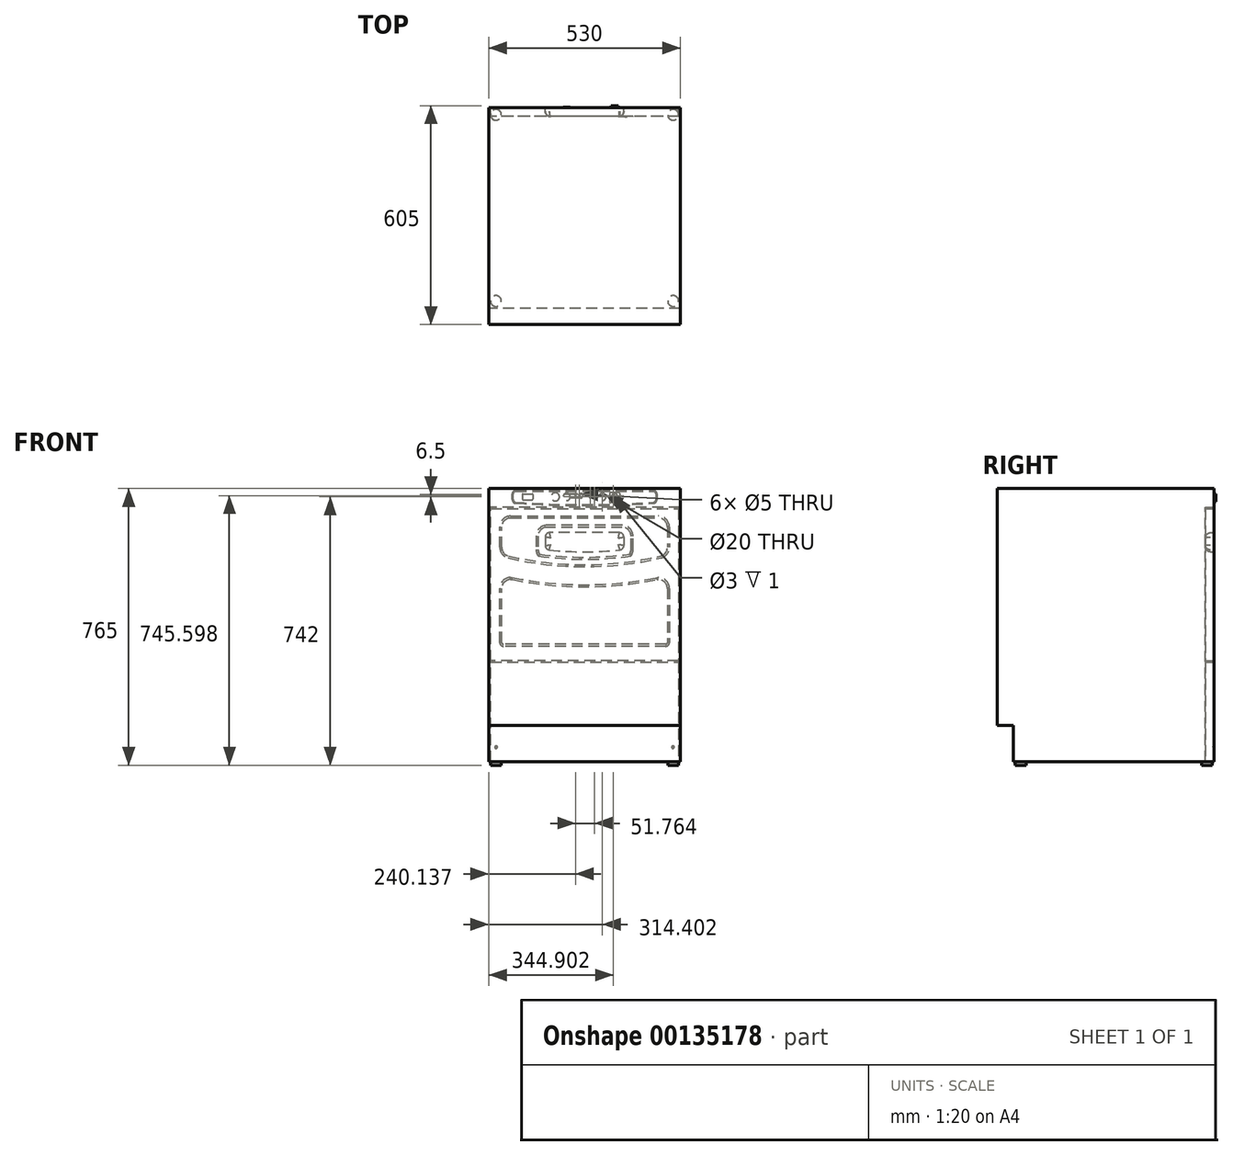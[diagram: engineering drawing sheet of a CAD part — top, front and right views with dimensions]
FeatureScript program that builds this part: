
annotation { "Feature Type Name" : "Feature", "Feature Type Description" : "" }
export const myFeature = defineFeature(function(context is Context, id is Id, definition is map)
    precondition{}
    {
        {
            var Q0;
            Q0=qCreatedBy(makeId("Right.planeOp"),FACE);
            var sketch = newSketch(context, id + "F0", { "sketchPlane" : qUnion([Q0])});
            skLineSegment(sketch, "E0", {"start": v(0, 0) * mm, "end": v(0, 755) * mm});
            skLineSegment(sketch, "E1", {"start": v(0, 755) * mm, "end": v(-600, 755) * mm});
            skLineSegment(sketch, "E2", {"start": v(-600, 755) * mm, "end": v(-600, 100) * mm});
            skLineSegment(sketch, "E3", {"start": v(-600, 100) * mm, "end": v(-555, 100) * mm});
            skLineSegment(sketch, "E4", {"start": v(-555, 100) * mm, "end": v(-555, 0) * mm});
            skLineSegment(sketch, "E5", {"start": v(-555, 0) * mm, "end": v(0, 0) * mm});
            skSolve(sketch);
        }
        {
            var Q0;
            Q0=qSketchRegion(id+"F0",true);
            extrude(context, id + "F1", {"entities" : qUnion([Q0]), "depth" : 530 * mm});
        }
        {
            var Q0;
            Q0=makeQuery(id+"F1.opExtrude","SWEPT_FACE",FACE,{"disambiguationData":[OSD([sQuery(id+"F0.wireOp",EDGE,"E5")])]});
            var sketch = newSketch(context, id + "F2", { "sketchPlane" : qUnion([Q0])});
            skCircle(sketch, "E6", {"center": v(510, 535) * mm, "radius": 15 * mm});
            skCircle(sketch, "E7", {"center": v(510, 20) * mm, "radius": 15 * mm});
            skCircle(sketch, "E8", {"center": v(20, 20) * mm, "radius": 15 * mm});
            skCircle(sketch, "E9", {"center": v(20, 535) * mm, "radius": 15 * mm});
            skSolve(sketch);
        }
        {
            var Q0;
            Q0=qSketchRegion(id+"F2",true);
            extrude(context, id + "F3", {"entities" : qUnion([Q0]), "operationType" : NewBodyOperationType.ADD, "depth" : 10 * mm});
        }
        {
            var Q0;
            Q0=makeQuery(id+"F1.opExtrude","SWEPT_FACE",FACE,{"disambiguationData":[OSD([sQuery(id+"F0.wireOp",EDGE,"E0")])]});
            var sketch = newSketch(context, id + "F4", { "sketchPlane" : qUnion([Q0])});
            skLineSegment(sketch, "E10", {"start": v(-528.5, 0) * mm, "end": v(-528.5, 703) * mm});
            skLineSegment(sketch, "E11", {"start": v(-528.5, 703) * mm, "end": v(-1.5, 703) * mm});
            skLineSegment(sketch, "E12", {"start": v(-1.5, 703) * mm, "end": v(-1.5, 0) * mm});
            skLineSegment(sketch, "E13", {"start": v(-1.5, 0) * mm, "end": v(-5.5, 0) * mm});
            skLineSegment(sketch, "E14", {"start": v(-5.5, 0) * mm, "end": v(-5.5, 275) * mm});
            skLineSegment(sketch, "E15", {"start": v(-5.5, 275) * mm, "end": v(-524.5, 275) * mm});
            skLineSegment(sketch, "E16", {"start": v(-524.5, 275) * mm, "end": v(-524.5, 0) * mm});
            skLineSegment(sketch, "E17", {"start": v(-524.5, 0) * mm, "end": v(-528.5, 0) * mm});
            skLineSegment(sketch, "E18", {"start": v(-524.5, 279) * mm, "end": v(-5.5, 279) * mm});
            skLineSegment(sketch, "E19", {"start": v(-5.5, 279) * mm, "end": v(-5.5, 699) * mm});
            skLineSegment(sketch, "E20", {"start": v(-5.5, 699) * mm, "end": v(-524.5, 699) * mm});
            skLineSegment(sketch, "E21", {"start": v(-524.5, 699) * mm, "end": v(-524.5, 279) * mm});
            skSolve(sketch);
        }
        {
            var Q0;
            Q0=qSketchRegion(id+"F4",true);
            extrude(context, id + "F5", {"entities" : qUnion([Q0]), "operationType" : NewBodyOperationType.REMOVE, "oppositeDirection" : true, "depth" : 25 * mm});
        }
        {
            var Q0;
            Q0=makeQuery(id+"F5.boolean.opBoolean","SPLIT",FACE,{"disambiguationData":[TD([makeQuery(id+"F5.opExtrude","SWEPT_FACE",FACE,{"disambiguationData":[OSD([sQuery(id+"F4.wireOp",EDGE,"E14")])]})])],"derivedFrom":makeQuery(id+"F1.opExtrude","SWEPT_FACE",FACE,{"disambiguationData":[OSD([sQuery(id+"F0.wireOp",EDGE,"E0")])]})});
            var sketch = newSketch(context, id + "F6", { "sketchPlane" : qUnion([Q0])});
            skCircle(sketch, "E22", {"center": v(-509.5, 40) * mm, "radius": 3.5 * mm});
            skCircle(sketch, "E23", {"center": v(-20.5, 40) * mm, "radius": 3.5 * mm});
            skSolve(sketch);
        }
        {
            var Q0;
            Q0=qSketchRegion(id+"F6",true);
            extrude(context, id + "F7", {"entities" : qUnion([Q0]), "operationType" : NewBodyOperationType.REMOVE, "oppositeDirection" : true, "depth" : 3 * mm, "hasDraft" : true, "draftAngle" : 45 * degree, "draftPullDirection" : true});
        }
        {
            var Q0;
            Q0=makeQuery(id+"F5.boolean.opBoolean","SPLIT",FACE,{"disambiguationData":[TD([makeQuery(id+"F5.opExtrude","SWEPT_FACE",FACE,{"disambiguationData":[OSD([sQuery(id+"F4.wireOp",EDGE,"E18")])]})])],"derivedFrom":makeQuery(id+"F1.opExtrude","SWEPT_FACE",FACE,{"disambiguationData":[OSD([sQuery(id+"F0.wireOp",EDGE,"E0")])]})});
            var sketch = newSketch(context, id + "F8", { "sketchPlane" : qUnion([Q0])});
            skLineSegment(sketch, "E24", {"start": v(-489.5, 319) * mm, "end": v(-40.5, 319) * mm});
            skLineSegment(sketch, "E25", {"start": v(-30.5, 329) * mm, "end": v(-30.5, 479) * mm});
            skLineSegment(sketch, "E26", {"start": v(-60.5, 509) * mm, "end": v(-65.5, 509) * mm});
            skLineSegment(sketch, "E27", {"start": v(-499.5, 329) * mm, "end": v(-499.5, 479) * mm});
            skLineSegment(sketch, "E28", {"start": v(-469.5, 509) * mm, "end": v(-464.5, 509) * mm});
            skArc(sketch, "E29", {"start": v(-464.5, 509) * mm, "mid": v(-265, 489) * mm, "end": v(-65.5, 509) * mm});
            skPoint(sketch, "E30.visualSharp", {"position": v(-499.5, 319) * mm});
            skArc(sketch, "E30.filletArc", {"start": v(-499.5, 329) * mm, "mid": v(-496.57, 321.93) * mm, "end": v(-489.5, 319) * mm});
            skPoint(sketch, "E31.visualSharp", {"position": v(-30.5, 319) * mm});
            skArc(sketch, "E31.filletArc", {"start": v(-40.5, 319) * mm, "mid": v(-33.43, 321.93) * mm, "end": v(-30.5, 329) * mm});
            skPoint(sketch, "E32.visualSharp", {"position": v(-30.5, 509) * mm});
            skArc(sketch, "E32.filletArc", {"start": v(-30.5, 479) * mm, "mid": v(-39.29, 500.21) * mm, "end": v(-60.5, 509) * mm});
            skPoint(sketch, "E33.visualSharp", {"position": v(-499.5, 509) * mm});
            skArc(sketch, "E33.filletArc", {"start": v(-469.5, 509) * mm, "mid": v(-490.71, 500.21) * mm, "end": v(-499.5, 479) * mm});
            skSolve(sketch);
        }
        {
            var Q0;
            Q0=qSketchRegion(id+"F8",true);
            extrude(context, id + "F9", {"entities" : qUnion([Q0]), "operationType" : NewBodyOperationType.REMOVE, "oppositeDirection" : true, "depth" : 2 * mm, "hasDraft" : true, "draftAngle" : 70 * degree, "draftPullDirection" : true});
        }
        {
            var Q0;
            Q0=makeQuery(id+"F5.boolean.opBoolean","SPLIT",FACE,{"disambiguationData":[TD([makeQuery(id+"F5.opExtrude","SWEPT_FACE",FACE,{"disambiguationData":[OSD([sQuery(id+"F4.wireOp",EDGE,"E18")])]})])],"derivedFrom":makeQuery(id+"F1.opExtrude","SWEPT_FACE",FACE,{"disambiguationData":[OSD([sQuery(id+"F0.wireOp",EDGE,"E0")])]})});
            var sketch = newSketch(context, id + "F10", { "sketchPlane" : qUnion([Q0])});
            skLineSegment(sketch, "E34", {"start": v(-499.5, 649) * mm, "end": v(-499.5, 592.5) * mm});
            skLineSegment(sketch, "E35", {"start": v(-469.5, 679) * mm, "end": v(-60.5, 679) * mm});
            skLineSegment(sketch, "E36", {"start": v(-30.5, 649) * mm, "end": v(-30.5, 592.5) * mm});
            skArc(sketch, "E37", {"start": v(-476.3, 563.28) * mm, "mid": v(-265, 539) * mm, "end": v(-53.7, 563.28) * mm});
            skPoint(sketch, "E38.visualSharp", {"position": v(-499.5, 679) * mm});
            skArc(sketch, "E38.filletArc", {"start": v(-469.5, 679) * mm, "mid": v(-490.71, 670.21) * mm, "end": v(-499.5, 649) * mm});
            skPoint(sketch, "E39.visualSharp", {"position": v(-30.5, 679) * mm});
            skArc(sketch, "E39.filletArc", {"start": v(-30.5, 649) * mm, "mid": v(-39.29, 670.21) * mm, "end": v(-60.5, 679) * mm});
            skPoint(sketch, "E40.visualSharp", {"position": v(-499.5, 569) * mm});
            skArc(sketch, "E40.filletArc", {"start": v(-499.5, 592.5) * mm, "mid": v(-493, 573.85) * mm, "end": v(-476.3, 563.28) * mm});
            skPoint(sketch, "E41.visualSharp", {"position": v(-30.5, 569) * mm});
            skArc(sketch, "E41.filletArc", {"start": v(-53.7, 563.28) * mm, "mid": v(-37, 573.85) * mm, "end": v(-30.5, 592.5) * mm});
            skSolve(sketch);
        }
        {
            var Q0;
            Q0=qSketchRegion(id+"F10",true);
            extrude(context, id + "F11", {"entities" : qUnion([Q0]), "operationType" : NewBodyOperationType.REMOVE, "oppositeDirection" : true, "depth" : 2 * mm, "hasDraft" : true, "draftAngle" : 70 * degree, "draftPullDirection" : true});
        }
        {
            var Q0;
            Q0=makeQuery(id+"F11.boolean.opBoolean","COPY",FACE,{"derivedFrom":makeQuery(id+"F11.opExtrude","CAP_FACE",FACE,{"disambiguationData":[OSD([sQuery(id+"F10.wireOp",EDGE,"E34"),sQuery(id+"F10.wireOp",EDGE,"E35"),sQuery(id+"F10.wireOp",EDGE,"E36"),sQuery(id+"F10.wireOp",EDGE,"E37"),sQuery(id+"F10.wireOp",EDGE,"E38.filletArc"),sQuery(id+"F10.wireOp",EDGE,"E39.filletArc"),sQuery(id+"F10.wireOp",EDGE,"E40.filletArc"),sQuery(id+"F10.wireOp",EDGE,"E41.filletArc")])],"isStart":false})});
            var sketch = newSketch(context, id + "F12", { "sketchPlane" : qUnion([Q0])});
            skLineSegment(sketch, "E42.bottom", {"start": v(-369, 653.5) * mm, "end": v(-161, 653.5) * mm});
            skLineSegment(sketch, "E42.left", {"start": v(-399, 623.5) * mm, "end": v(-399, 586.76) * mm});
            skLineSegment(sketch, "E42.right", {"start": v(-131, 623.5) * mm, "end": v(-131, 586.76) * mm});
            skPoint(sketch, "E43.visualSharp", {"position": v(-399, 629.5) * mm});
            skArc(sketch, "E43.filletArc", {"start": v(-399, 586.76) * mm, "mid": v(-397.41, 577.12) * mm, "end": v(-392.8, 568.5) * mm});
            skPoint(sketch, "E44.visualSharp", {"position": v(-399, 653.5) * mm});
            skArc(sketch, "E44.filletArc", {"start": v(-369, 653.5) * mm, "mid": v(-390.22, 644.72) * mm, "end": v(-399, 623.5) * mm});
            skPoint(sketch, "E45.visualSharp", {"position": v(-131, 653.5) * mm});
            skArc(sketch, "E45.filletArc", {"start": v(-131, 623.5) * mm, "mid": v(-139.78, 644.72) * mm, "end": v(-161, 653.5) * mm});
            skPoint(sketch, "E46.visualSharp", {"position": v(-131, 629.5) * mm});
            skArc(sketch, "E46.filletArc", {"start": v(-137.2, 568.5) * mm, "mid": v(-132.59, 577.12) * mm, "end": v(-131, 586.76) * mm});
            skArc(sketch, "E47", {"start": v(-392.8, 568.5) * mm, "mid": v(-265, 559.5) * mm, "end": v(-137.2, 568.5) * mm});
            skSolve(sketch);
        }
        {
            var Q0;
            Q0=qSketchRegion(id+"F12",true);
            extrude(context, id + "F13", {"entities" : qUnion([Q0]), "operationType" : NewBodyOperationType.ADD, "depth" : 2 * mm, "hasDraft" : true, "draftAngle" : 70 * degree, "draftPullDirection" : true});
        }
        {
            var Q0;
            Q0=makeQuery(id+"F13.opExtrude","CAP_FACE",FACE,{"disambiguationData":[OSD([sQuery(id+"F12.wireOp",EDGE,"E42.bottom"),sQuery(id+"F12.wireOp",EDGE,"E42.left"),sQuery(id+"F12.wireOp",EDGE,"E42.right"),sQuery(id+"F12.wireOp",EDGE,"E43.filletArc"),sQuery(id+"F12.wireOp",EDGE,"E44.filletArc"),sQuery(id+"F12.wireOp",EDGE,"E45.filletArc"),sQuery(id+"F12.wireOp",EDGE,"E46.filletArc"),sQuery(id+"F12.wireOp",EDGE,"E47")])],"isStart":false});
            var sketch = newSketch(context, id + "F14", { "sketchPlane" : qUnion([Q0])});
            skLineSegment(sketch, "E48.bottom", {"start": v(-361.51, 633.01) * mm, "end": v(-168.49, 633.01) * mm});
            skLineSegment(sketch, "E48.left", {"start": v(-373.51, 621.01) * mm, "end": v(-373.51, 597.3) * mm});
            skLineSegment(sketch, "E48.right", {"start": v(-156.49, 621.01) * mm, "end": v(-156.49, 597.3) * mm});
            skPoint(sketch, "E49.visualSharp", {"position": v(-373.51, 633.01) * mm});
            skArc(sketch, "E49.filletArc", {"start": v(-361.51, 633.01) * mm, "mid": v(-370, 629.5) * mm, "end": v(-373.51, 621.01) * mm});
            skPoint(sketch, "E50.visualSharp", {"position": v(-156.49, 633.01) * mm});
            skArc(sketch, "E50.filletArc", {"start": v(-156.49, 621.01) * mm, "mid": v(-160, 629.5) * mm, "end": v(-168.49, 633.01) * mm});
            skArc(sketch, "E51", {"start": v(-362.83, 585.38) * mm, "mid": v(-265, 579.99) * mm, "end": v(-167.17, 585.38) * mm});
            skPoint(sketch, "E52.visualSharp", {"position": v(-373.51, 586.63) * mm});
            skArc(sketch, "E52.filletArc", {"start": v(-373.51, 597.3) * mm, "mid": v(-370.45, 589.3) * mm, "end": v(-362.83, 585.38) * mm});
            skPoint(sketch, "E53.visualSharp", {"position": v(-156.49, 586.63) * mm});
            skArc(sketch, "E53.filletArc", {"start": v(-167.17, 585.38) * mm, "mid": v(-159.55, 589.3) * mm, "end": v(-156.49, 597.3) * mm});
            skSolve(sketch);
        }
        {
            var Q0;
            Q0=qSketchRegion(id+"F14",true);
            extrude(context, id + "F15", {"entities" : qUnion([Q0]), "operationType" : NewBodyOperationType.REMOVE, "oppositeDirection" : true, "depth" : 25 * mm});
        }
        {
            var Q0;
            Q0=makeQuery(id+"F15.boolean.opBoolean","COPY",EDGE,{"derivedFrom":makeQuery(id+"F15.opExtrude","CAP_EDGE",EDGE,{"disambiguationData":[OSD([sQuery(id+"F14.wireOp",EDGE,"E48.left")])],"isStart":false})});
            fillet(context, id + "F16", {"entities" : qUnion([Q0]), "radius" : 15 * mm, "tangentPropagation" : true, "allowEdgeOverflow" : false});
        }
        {
            var Q0;
            {var subQ1=sQuery(id+"F0.wireOp",EDGE,"E1");var subQ5=sQuery(id+"F0.wireOp",EDGE,"E0");Q0=makeQuery(id+"F5.boolean.opBoolean","SPLIT",FACE,{"disambiguationData":[TD([makeQuery(id+"F1.opExtrude","SWEPT_FACE",FACE,{"disambiguationData":[OSD([subQ1])]})])],"derivedFrom":makeQuery(id+"F1.opExtrude","SWEPT_FACE",FACE,{"disambiguationData":[OSD([subQ5])]})});}
            var sketch = newSketch(context, id + "F17", { "sketchPlane" : qUnion([Q0])});
            skLineSegment(sketch, "E54.bottom", {"start": v(-455, 750) * mm, "end": v(-75, 750) * mm});
            skLineSegment(sketch, "E54.left", {"start": v(-465, 740) * mm, "end": v(-465, 724.34) * mm});
            skLineSegment(sketch, "E54.right", {"start": v(-65, 740) * mm, "end": v(-65, 724.34) * mm});
            skArc(sketch, "E55", {"start": v(-455.67, 714.36) * mm, "mid": v(-265, 708) * mm, "end": v(-74.33, 714.36) * mm});
            skPoint(sketch, "E56.visualSharp", {"position": v(-465, 750) * mm});
            skArc(sketch, "E56.filletArc", {"start": v(-455, 750) * mm, "mid": v(-462.07, 747.07) * mm, "end": v(-465, 740) * mm});
            skPoint(sketch, "E57.visualSharp", {"position": v(-65, 750) * mm});
            skArc(sketch, "E57.filletArc", {"start": v(-65, 740) * mm, "mid": v(-67.93, 747.07) * mm, "end": v(-75, 750) * mm});
            skPoint(sketch, "E58.visualSharp", {"position": v(-465, 715) * mm});
            skArc(sketch, "E58.filletArc", {"start": v(-465, 724.34) * mm, "mid": v(-462.3, 717.5) * mm, "end": v(-455.67, 714.36) * mm});
            skPoint(sketch, "E59.visualSharp", {"position": v(-65, 715) * mm});
            skArc(sketch, "E59.filletArc", {"start": v(-74.33, 714.36) * mm, "mid": v(-67.7, 717.5) * mm, "end": v(-65, 724.34) * mm});
            skSolve(sketch);
        }
        {
            var Q0;
            Q0=makeQuery(id+"F17.imprint","IMPRINT",FACE,{"disambiguationData":[TD([[makeQuery(id+"F17.imprint","IMPRINT",EDGE,{"derivedFrom":sQuery(id+"F17.wireOp",EDGE,"E54.bottom")}),-1.0]])]});
            extrude(context, id + "F18", {"entities" : qUnion([Q0]), "operationType" : NewBodyOperationType.REMOVE, "depth" : 1 * mm});
        }
        {
            var Q0;
            Q0=qSketchRegion(id+"F17",true);
            extrude(context, id + "F19", {"entities" : qUnion([Q0]), "operationType" : NewBodyOperationType.REMOVE, "oppositeDirection" : true, "depth" : 1.5 * mm, "hasDraft" : true, "draftAngle" : 60 * degree, "draftPullDirection" : true});
        }
        {
            var Q0;
            Q0=makeQuery(id+"F19.boolean.opBoolean","COPY",FACE,{"derivedFrom":makeQuery(id+"F19.opExtrude","CAP_FACE",FACE,{"disambiguationData":[OSD([sQuery(id+"F17.wireOp",EDGE,"E54.bottom"),sQuery(id+"F17.wireOp",EDGE,"E54.left"),sQuery(id+"F17.wireOp",EDGE,"E54.right"),sQuery(id+"F17.wireOp",EDGE,"E55"),sQuery(id+"F17.wireOp",EDGE,"E56.filletArc"),sQuery(id+"F17.wireOp",EDGE,"E57.filletArc"),sQuery(id+"F17.wireOp",EDGE,"E58.filletArc"),sQuery(id+"F17.wireOp",EDGE,"E59.filletArc")])],"isStart":false})});
            var sketch = newSketch(context, id + "F20", { "sketchPlane" : qUnion([Q0])});
            skLineSegment(sketch, "E60.bottom", {"start": v(-362.4, 743.6) * mm, "end": v(-334.4, 743.6) * mm});
            skLineSegment(sketch, "E60.top", {"start": v(-362.4, 715.6) * mm, "end": v(-334.4, 715.6) * mm});
            skLineSegment(sketch, "E60.left", {"start": v(-362.4, 743.6) * mm, "end": v(-362.4, 715.6) * mm});
            skLineSegment(sketch, "E60.right", {"start": v(-334.4, 743.6) * mm, "end": v(-334.4, 715.6) * mm});
            skSolve(sketch);
        }
        {
            var Q0;
            Q0=qSketchRegion(id+"F20",true);
            extrude(context, id + "F21", {"entities" : qUnion([Q0]), "depth" : 1.5 * mm});
        }
        {
            var Q0;
            Q0=makeQuery(id+"F21.opExtrude","SWEPT_EDGE",EDGE,{"disambiguationData":[OSD([sQuery(id+"F20.wireOp",EDGE,"E60.bottom"),sQuery(id+"F20.wireOp",EDGE,"E60.left")])]});
            var Q1;
            Q1=makeQuery(id+"F21.opExtrude","SWEPT_EDGE",EDGE,{"disambiguationData":[OSD([sQuery(id+"F20.wireOp",EDGE,"E60.bottom"),sQuery(id+"F20.wireOp",EDGE,"E60.right")])]});
            var Q2;
            Q2=makeQuery(id+"F21.opExtrude","SWEPT_EDGE",EDGE,{"disambiguationData":[OSD([sQuery(id+"F20.wireOp",EDGE,"E60.top"),sQuery(id+"F20.wireOp",EDGE,"E60.right")])]});
            var Q3;
            Q3=makeQuery(id+"F21.opExtrude","SWEPT_EDGE",EDGE,{"disambiguationData":[OSD([sQuery(id+"F20.wireOp",EDGE,"E60.top"),sQuery(id+"F20.wireOp",EDGE,"E60.left")])]});
            fillet(context, id + "F22", {"entities" : qUnion([Q0, Q1, Q2, Q3]), "radius" : 2 * mm, "tangentPropagation" : true, "allowEdgeOverflow" : false});
        }
        {
            var Q0;
            Q0=makeQuery(id+"F21.opExtrude","CAP_EDGE",EDGE,{"disambiguationData":[OSD([sQuery(id+"F20.wireOp",EDGE,"E60.left")])],"isStart":false});
            fillet(context, id + "F23", {"entities" : qUnion([Q0]), "radius" : 0.5 * mm, "tangentPropagation" : true, "allowEdgeOverflow" : false});
        }
        {
            var Q0;
            Q0=makeQuery(id+"F21.opExtrude","CAP_FACE",FACE,{"disambiguationData":[OSD([sQuery(id+"F20.wireOp",EDGE,"E60.bottom"),sQuery(id+"F20.wireOp",EDGE,"E60.top"),sQuery(id+"F20.wireOp",EDGE,"E60.left"),sQuery(id+"F20.wireOp",EDGE,"E60.right")])],"isStart":false});
            var sketch = newSketch(context, id + "F24", { "sketchPlane" : qUnion([Q0])});
            skCircle(sketch, "E61", {"center": v(-348.4, 729.6) * mm, "radius": 10.5 * mm});
            skPoint(sketch, "E61.centerSnap0", {"position": v(-348.4, 743.1) * mm});
            skPoint(sketch, "E61.centerSnap1", {"position": v(-361.9, 729.6) * mm});
            skSolve(sketch);
        }
        {
            var Q0;
            Q0=qSketchRegion(id+"F24",true);
            extrude(context, id + "F25", {"entities" : qUnion([Q0]), "depth" : 5 * mm});
        }
        {
            var Q0;
            Q0=makeQuery(id+"F25.opExtrude","CAP_FACE",FACE,{"disambiguationData":[OSD([sQuery(id+"F24.wireOp",EDGE,"E61")])],"isStart":false});
            var sketch = newSketch(context, id + "F26", { "sketchPlane" : qUnion([Q0])});
            skCircle(sketch, "E62", {"center": v(-344.9, 735.6) * mm, "radius": 1.5 * mm});
            skSolve(sketch);
        }
        {
            var Q0;
            Q0=qSketchRegion(id+"F26",true);
            extrude(context, id + "F27", {"entities" : qUnion([Q0]), "operationType" : NewBodyOperationType.REMOVE, "oppositeDirection" : true, "depth" : 1 * mm});
        }
        {
            var Q0;
            Q0=makeQuery(id+"F19.boolean.opBoolean","COPY",FACE,{"derivedFrom":makeQuery(id+"F19.opExtrude","CAP_FACE",FACE,{"disambiguationData":[OSD([sQuery(id+"F17.wireOp",EDGE,"E54.bottom"),sQuery(id+"F17.wireOp",EDGE,"E54.left"),sQuery(id+"F17.wireOp",EDGE,"E54.right"),sQuery(id+"F17.wireOp",EDGE,"E55"),sQuery(id+"F17.wireOp",EDGE,"E56.filletArc"),sQuery(id+"F17.wireOp",EDGE,"E57.filletArc"),sQuery(id+"F17.wireOp",EDGE,"E58.filletArc"),sQuery(id+"F17.wireOp",EDGE,"E59.filletArc")])],"isStart":false})});
            var sketch = newSketch(context, id + "F28", { "sketchPlane" : qUnion([Q0])});
            skLineSegment(sketch, "E63.bottom", {"start": v(-94.6, 740.17) * mm, "end": v(-120.6, 740.17) * mm});
            skLineSegment(sketch, "E63.top", {"start": v(-94.6, 724.17) * mm, "end": v(-120.6, 724.17) * mm});
            skLineSegment(sketch, "E63.left", {"start": v(-92.6, 738.17) * mm, "end": v(-92.6, 726.17) * mm});
            skLineSegment(sketch, "E63.right", {"start": v(-122.6, 738.17) * mm, "end": v(-122.6, 726.17) * mm});
            skPoint(sketch, "E64.visualSharp", {"position": v(-92.6, 740.17) * mm});
            skArc(sketch, "E64.filletArc", {"start": v(-92.6, 738.17) * mm, "mid": v(-93.18, 739.58) * mm, "end": v(-94.6, 740.17) * mm});
            skPoint(sketch, "E65.visualSharp", {"position": v(-92.6, 724.17) * mm});
            skArc(sketch, "E65.filletArc", {"start": v(-94.6, 724.17) * mm, "mid": v(-93.18, 724.76) * mm, "end": v(-92.6, 726.17) * mm});
            skPoint(sketch, "E66.visualSharp", {"position": v(-122.6, 724.17) * mm});
            skArc(sketch, "E66.filletArc", {"start": v(-122.6, 726.17) * mm, "mid": v(-122.01, 724.76) * mm, "end": v(-120.6, 724.17) * mm});
            skPoint(sketch, "E67.visualSharp", {"position": v(-122.6, 740.17) * mm});
            skArc(sketch, "E67.filletArc", {"start": v(-120.6, 740.17) * mm, "mid": v(-122.01, 739.58) * mm, "end": v(-122.6, 738.17) * mm});
            skSolve(sketch);
        }
        {
            var Q0;
            Q0=qSketchRegion(id+"F28",true);
            extrude(context, id + "F29", {"entities" : qUnion([Q0]), "depth" : 1.5 * mm});
        }
        {
            var Q0;
            Q0=makeQuery(id+"F29.opExtrude","CAP_EDGE",EDGE,{"disambiguationData":[OSD([sQuery(id+"F28.wireOp",EDGE,"E63.right")])],"isStart":false});
            fillet(context, id + "F30", {"entities" : qUnion([Q0]), "radius" : 1.5 * mm, "tangentPropagation" : true, "allowEdgeOverflow" : false});
        }
        {
            var Q0;
            Q0=makeQuery(id+"F19.boolean.opBoolean","COPY",FACE,{"derivedFrom":makeQuery(id+"F19.opExtrude","CAP_FACE",FACE,{"disambiguationData":[OSD([sQuery(id+"F17.wireOp",EDGE,"E54.bottom"),sQuery(id+"F17.wireOp",EDGE,"E54.left"),sQuery(id+"F17.wireOp",EDGE,"E54.right"),sQuery(id+"F17.wireOp",EDGE,"E55"),sQuery(id+"F17.wireOp",EDGE,"E56.filletArc"),sQuery(id+"F17.wireOp",EDGE,"E57.filletArc"),sQuery(id+"F17.wireOp",EDGE,"E58.filletArc"),sQuery(id+"F17.wireOp",EDGE,"E59.filletArc")])],"isStart":false})});
            var sketch = newSketch(context, id + "F31", { "sketchPlane" : qUnion([Q0])});
            skCircle(sketch, "E68", {"center": v(-184.1, 732) * mm, "radius": 11.5 * mm});
            skCircle(sketch, "E69", {"center": v(-215.6, 732) * mm, "radius": 10 * mm});
            skLineSegment(sketch, "E70", {"start": v(-215.6, 742) * mm, "end": v(-253.64, 742) * mm});
            skLineSegment(sketch, "E71", {"start": v(-260.14, 735.5) * mm, "end": v(-260.14, 735.5) * mm});
            skLineSegment(sketch, "E72", {"start": v(-253.64, 729) * mm, "end": v(-225.14, 729) * mm});
            skPoint(sketch, "E73.visualSharp", {"position": v(-260.14, 742) * mm});
            skArc(sketch, "E73.filletArc", {"start": v(-253.64, 742) * mm, "mid": v(-258.23, 740.1) * mm, "end": v(-260.14, 735.5) * mm});
            skPoint(sketch, "E74.visualSharp", {"position": v(-260.14, 729) * mm});
            skArc(sketch, "E74.filletArc", {"start": v(-260.14, 735.5) * mm, "mid": v(-258.23, 730.9) * mm, "end": v(-253.64, 729) * mm});
            skCircle(sketch, "E75", {"center": v(-251.14, 738.5) * mm, "radius": 2.5 * mm});
            skCircle(sketch, "E76", {"center": v(-240.14, 738.5) * mm, "radius": 2.5 * mm});
            skCircle(sketch, "E77", {"center": v(-240.14, 732.5) * mm, "radius": 2.5 * mm});
            skCircle(sketch, "E78", {"center": v(-251.14, 732.5) * mm, "radius": 2.5 * mm});
            skSolve(sketch);
        }
        {
            var Q0;
            {var subQ4=sQuery(id+"F17.wireOp",EDGE,"E56.filletArc");var subQ5=sQuery(id+"F17.wireOp",EDGE,"E54.right");var subQ6=sQuery(id+"F17.wireOp",EDGE,"E55");var subQ7=sQuery(id+"F17.wireOp",EDGE,"E54.bottom");var subQ8=sQuery(id+"F17.wireOp",EDGE,"E54.left");var subQ9=sQuery(id+"F17.wireOp",EDGE,"E59.filletArc");var subQ10=sQuery(id+"F17.wireOp",EDGE,"E57.filletArc");var subQ11=sQuery(id+"F17.wireOp",EDGE,"E58.filletArc");Q0=makeQuery(id+"FWKtfQyY8KCrMXJ_1.boolean.opBoolean","SPLIT",FACE,{"disambiguationData":[TD([makeQuery(id+"F19.boolean.opBoolean","COPY",FACE,{"derivedFrom":makeQuery(id+"F19.opExtrude","SWEPT_FACE",FACE,{"disambiguationData":[OSD([subQ7])]})})])],"derivedFrom":makeQuery(id+"F19.boolean.opBoolean","COPY",FACE,{"derivedFrom":makeQuery(id+"F19.opExtrude","CAP_FACE",FACE,{"disambiguationData":[OSD([subQ7,subQ8,subQ5,subQ6,subQ4,subQ10,subQ11,subQ9])],"isStart":false})})});}
            var sketch = newSketch(context, id + "F32", { "sketchPlane" : qUnion([Q0])});
            skCircle(sketch, "E79", {"center": v(-280.9, 732) * mm, "radius": 2.5 * mm});
            skCircle(sketch, "E80", {"center": v(-291.9, 732) * mm, "radius": 2.5 * mm});
            skCircle(sketch, "E81", {"center": v(-314.4, 732) * mm, "radius": 10 * mm});
            skSolve(sketch);
        }
        {
            var Q0;
            Q0=qSketchRegion(id+"F32",true);
            extrude(context, id + "F33", {"entities" : qUnion([Q0]), "operationType" : NewBodyOperationType.ADD, "depth" : 1 * mm});
        }
        {
            var Q0;
            {var subQ4=sQuery(id+"F17.wireOp",EDGE,"E56.filletArc");var subQ5=sQuery(id+"F17.wireOp",EDGE,"E54.right");var subQ6=sQuery(id+"F17.wireOp",EDGE,"E55");var subQ7=sQuery(id+"F17.wireOp",EDGE,"E54.bottom");var subQ8=sQuery(id+"F17.wireOp",EDGE,"E54.left");var subQ9=sQuery(id+"F17.wireOp",EDGE,"E59.filletArc");var subQ10=sQuery(id+"F17.wireOp",EDGE,"E57.filletArc");var subQ11=sQuery(id+"F17.wireOp",EDGE,"E58.filletArc");Q0=makeQuery(id+"FWKtfQyY8KCrMXJ_1.boolean.opBoolean","SPLIT",FACE,{"disambiguationData":[TD([makeQuery(id+"F19.boolean.opBoolean","COPY",FACE,{"derivedFrom":makeQuery(id+"F19.opExtrude","SWEPT_FACE",FACE,{"disambiguationData":[OSD([subQ7])]})})])],"derivedFrom":makeQuery(id+"F19.boolean.opBoolean","COPY",FACE,{"derivedFrom":makeQuery(id+"F19.opExtrude","CAP_FACE",FACE,{"disambiguationData":[OSD([subQ7,subQ8,subQ5,subQ6,subQ4,subQ10,subQ11,subQ9])],"isStart":false})})});}
            extrude(context, id + "F34", {"entities" : qUnion([Q0]), "depth" : 0.1 * mm});
        }
        {
            var Q0;
            {var subQ0=sQuery(id+"F31.wireOp",EDGE,"E69");var subQ1=makeQuery(id+"F31.imprint","INTERSECT",VERTEX,{"derivedFrom":[subQ0,sQuery(id+"F31.wireOp",EDGE,"E70")]});Q0=makeQuery(id+"F31.imprint","IMPRINT",FACE,{"disambiguationData":[TD([[makeQuery(id+"F31.imprint","IMPRINT",EDGE,{"disambiguationData":[TD([[subQ1,-1.0]])],"derivedFrom":subQ0}),1.0]])]});}
            extrude(context, id + "F35", {"entities" : qUnion([Q0]), "depth" : 2 * mm});
        }
        {
            var Q0;
            {var subQ1=sQuery(id+"F31.wireOp",EDGE,"E70");Q0=makeQuery(id+"F31.imprint","IMPRINT",FACE,{"disambiguationData":[TD([[makeQuery(id+"F31.imprint","IMPRINT",EDGE,{"derivedFrom":subQ1}),1.0]])]});}
            var Q1;
            Q1=makeQuery(id+"F31.imprint","IMPRINT",FACE,{"disambiguationData":[TD([[makeQuery(id+"F31.imprint","IMPRINT",EDGE,{"derivedFrom":sQuery(id+"F31.wireOp",EDGE,"E68")}),1.0]])]});
            extrude(context, id + "F36", {"entities" : qUnion([Q0, Q1]), "depth" : 1 * mm});
        }
        {
            var Q0;
            Q0=makeQuery(id+"F33.opExtrude","CAP_FACE",FACE,{"disambiguationData":[OSD([sQuery(id+"F32.wireOp",EDGE,"E81")])],"isStart":false});
            var Q1;
            Q1=makeQuery(id+"F33.opExtrude","CAP_FACE",FACE,{"disambiguationData":[OSD([sQuery(id+"F32.wireOp",EDGE,"E80")])],"isStart":false});
            var Q2;
            Q2=makeQuery(id+"F33.opExtrude","CAP_FACE",FACE,{"disambiguationData":[OSD([sQuery(id+"F32.wireOp",EDGE,"E79")])],"isStart":false});
            extrude(context, id + "F37", {"entities" : qUnion([Q0, Q1, Q2]), "depth" : 0.1 * mm});
        }
    });
